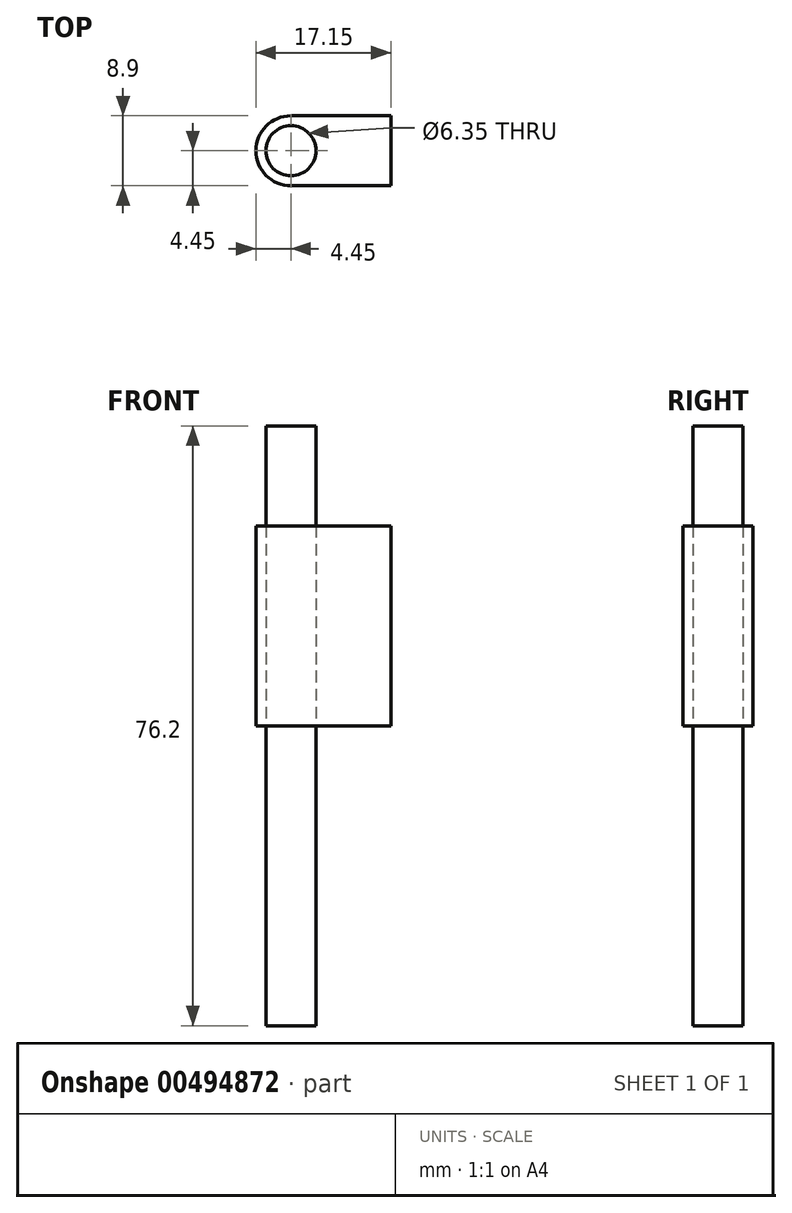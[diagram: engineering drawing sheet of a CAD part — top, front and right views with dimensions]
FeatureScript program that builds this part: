
annotation { "Feature Type Name" : "Feature", "Feature Type Description" : "" }
export const myFeature = defineFeature(function(context is Context, id is Id, definition is map)
    precondition{}
    {
        {
            var Q0;
            Q0=qCreatedBy(makeId("Top.planeOp"),FACE);
            var sketch = newSketch(context, id + "F0", { "sketchPlane" : qUnion([Q0])});
            skCircle(sketch, "E0", {"center": v(0, 0) * mm, "radius": 3.18 * mm});
            skArc(sketch, "E1", {"start": v(0, 4.45) * mm, "mid": v(-4.45, 0) * mm, "end": v(0, -4.45) * mm});
            skLineSegment(sketch, "E2", {"start": v(0, 4.45) * mm, "end": v(12.7, 4.45) * mm});
            skLineSegment(sketch, "E3", {"start": v(12.7, 4.45) * mm, "end": v(12.7, -4.44) * mm});
            skLineSegment(sketch, "E4", {"start": v(12.7, -4.44) * mm, "end": v(0, -4.45) * mm});
            skSolve(sketch);
        }
        {
            var Q0;
            Q0=makeQuery(id+"F0.imprint","IMPRINT",FACE,{"disambiguationData":[TD([[makeQuery(id+"F0.imprint","IMPRINT",EDGE,{"derivedFrom":sQuery(id+"F0.wireOp",EDGE,"E0")}),-1.0]])]});
            extrude(context, id + "F1", {"entities" : qUnion([Q0]), "depth" : 25.4 * mm});
        }
        {
            var Q0;
            Q0=makeQuery(id+"F0.imprint","IMPRINT",FACE,{"disambiguationData":[TD([[makeQuery(id+"F0.imprint","IMPRINT",EDGE,{"derivedFrom":sQuery(id+"F0.wireOp",EDGE,"E0")}),1.0]])]});
            extrude(context, id + "F2", {"entities" : qUnion([Q0]), "endBound" : BoundingType.SYMMETRIC, "depth" : 76.2 * mm});
        }
    });
